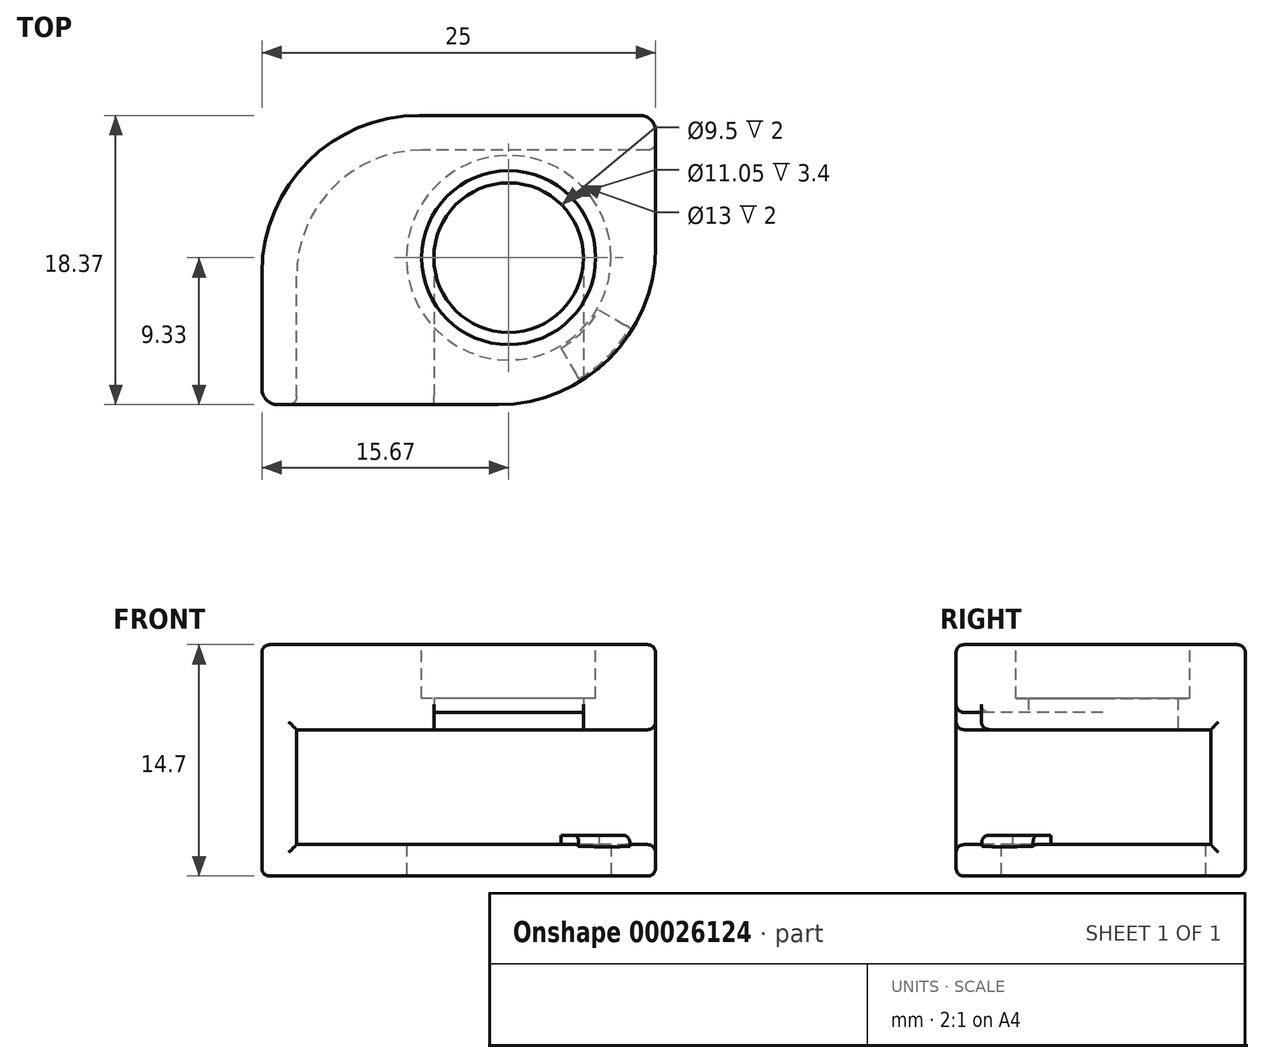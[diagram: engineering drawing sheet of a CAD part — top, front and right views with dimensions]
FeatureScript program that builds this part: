
annotation { "Feature Type Name" : "Feature", "Feature Type Description" : "" }
export const myFeature = defineFeature(function(context is Context, id is Id, definition is map)
    precondition{}
    {
        {
            var Q0;
            Q0=qCreatedBy(makeId("Top.planeOp"),FACE);
            var sketch = newSketch(context, id + "F0", { "sketchPlane" : qUnion([Q0])});
            skCircle(sketch, "E0", {"center": v(0, 0) * mm, "radius": 4.75 * mm});
            skLineSegment(sketch, "E1.bottom", {"start": v(-15.67, 9.04) * mm, "end": v(9.33, 9.04) * mm});
            skLineSegment(sketch, "E1.top", {"start": v(-15.67, -9.33) * mm, "end": v(9.33, -9.33) * mm});
            skLineSegment(sketch, "E1.left", {"start": v(-15.67, 9.04) * mm, "end": v(-15.67, -9.33) * mm});
            skLineSegment(sketch, "E1.right", {"start": v(9.33, 9.04) * mm, "end": v(9.33, -9.33) * mm});
            skSolve(sketch);
        }
        {
            var Q0;
            Q0 = qSketchRegion(id + "F0", true);
            extrude(context, id + "F1", {"entities" : qUnion([Q0]), "depth" : 5.4 * mm});
        }
        {
            var Q0;
            Q0=makeQuery(id+"F1.opExtrude","CAP_FACE",FACE,{"disambiguationData":[OSD([sQuery(id+"F0.wireOp",EDGE,"E0"),sQuery(id+"F0.wireOp",EDGE,"E1.bottom"),sQuery(id+"F0.wireOp",EDGE,"E1.top"),sQuery(id+"F0.wireOp",EDGE,"E1.left"),sQuery(id+"F0.wireOp",EDGE,"E1.right")])],"isStart":false});
            var sketch = newSketch(context, id + "F2", { "sketchPlane" : qUnion([Q0])});
            skCircle(sketch, "E2", {"center": v(0, 0) * mm, "radius": 5.53 * mm});
            skSolve(sketch);
        }
        {
            var Q0;
            Q0 = qSketchRegion(id + "F2", true);
            extrude(context, id + "F3", {"entities" : qUnion([Q0]), "operationType" : NewBodyOperationType.REMOVE, "oppositeDirection" : true, "depth" : 3.4 * mm});
        }
        {
            var Q0;
            Q0=makeQuery(id+"F1.opExtrude","SWEPT_EDGE",EDGE,{"disambiguationData":[OSD([sQuery(id+"F0.wireOp",EDGE,"E1.top"),sQuery(id+"F0.wireOp",EDGE,"E1.right")])]});
            fillet(context, id + "F4", {"entities" : qUnion([Q0]), "radius" : 10 * mm, "tangentPropagation" : true, "allowEdgeOverflow" : false});
        }
        {
            var Q0;
            Q0=makeQuery(id+"F1.opExtrude","CAP_FACE",FACE,{"disambiguationData":[OSD([sQuery(id+"F0.wireOp",EDGE,"E0"),sQuery(id+"F0.wireOp",EDGE,"E1.bottom"),sQuery(id+"F0.wireOp",EDGE,"E1.top"),sQuery(id+"F0.wireOp",EDGE,"E1.left"),sQuery(id+"F0.wireOp",EDGE,"E1.right")])],"isStart":true});
            var sketch = newSketch(context, id + "F5", { "sketchPlane" : qUnion([Q0])});
            skLineSegment(sketch, "E3.bottom", {"start": v(9.33, -9.04) * mm, "end": v(-15.67, -9.04) * mm});
            skLineSegment(sketch, "E3.top", {"start": v(9.33, -6.84) * mm, "end": v(-13.47, -6.84) * mm});
            skLineSegment(sketch, "E3.left", {"start": v(9.33, -9.04) * mm, "end": v(9.33, -6.84) * mm});
            skLineSegment(sketch, "E3.right", {"start": v(-15.67, -9.04) * mm, "end": v(-15.67, -6.84) * mm});
            skLineSegment(sketch, "E4.bottom", {"start": v(-15.67, 9.33) * mm, "end": v(-13.47, 9.33) * mm});
            skLineSegment(sketch, "E4.left", {"start": v(-15.67, 9.33) * mm, "end": v(-15.67, -6.84) * mm});
            skLineSegment(sketch, "E4.right", {"start": v(-13.47, 9.33) * mm, "end": v(-13.47, -6.84) * mm});
            skSolve(sketch);
        }
        {
            var Q0;
            Q0 = qSketchRegion(id + "F5", true);
            extrude(context, id + "F6", {"entities" : qUnion([Q0]), "operationType" : NewBodyOperationType.ADD, "depth" : 7.3 * mm});
        }
        {
            var Q0;
            Q0=makeQuery(id+"F6.opExtrude","SWEPT_EDGE",EDGE,{"disambiguationData":[OSD([sQuery(id+"F5.wireOp",EDGE,"E3.top"),sQuery(id+"F5.wireOp",EDGE,"E4.right")])]});
            fillet(context, id + "F7", {"entities" : qUnion([Q0]), "radius" : 8 * mm, "tangentPropagation" : true, "allowEdgeOverflow" : false});
        }
        {
            var Q0;
            Q0=makeQuery(id+"F6.opExtrude","CAP_FACE",FACE,{"disambiguationData":[OSD([sQuery(id+"F5.wireOp",EDGE,"E3.bottom"),sQuery(id+"F5.wireOp",EDGE,"E3.top"),sQuery(id+"F5.wireOp",EDGE,"E3.left"),sQuery(id+"F5.wireOp",EDGE,"E3.right"),sQuery(id+"F5.wireOp",EDGE,"E4.bottom"),sQuery(id+"F5.wireOp",EDGE,"E4.left"),sQuery(id+"F5.wireOp",EDGE,"E4.right")])],"isStart":false});
            var sketch = newSketch(context, id + "F8", { "sketchPlane" : qUnion([Q0])});
            skLineSegment(sketch, "E5.bottom", {"start": v(-15.67, -9.04) * mm, "end": v(9.33, -9.04) * mm});
            skLineSegment(sketch, "E5.top", {"start": v(-15.67, 9.33) * mm, "end": v(9.33, 9.33) * mm});
            skLineSegment(sketch, "E5.left", {"start": v(-15.67, -9.04) * mm, "end": v(-15.67, 9.33) * mm});
            skLineSegment(sketch, "E5.right", {"start": v(9.33, -9.04) * mm, "end": v(9.33, 9.33) * mm});
            skSolve(sketch);
        }
        {
            var Q0;
            Q0 = qSketchRegion(id + "F8", true);
            extrude(context, id + "F9", {"entities" : qUnion([Q0]), "operationType" : NewBodyOperationType.ADD, "depth" : 2 * mm});
        }
        {
            var Q0;
            Q0=makeQuery(id+"F9.opExtrude","SWEPT_EDGE",EDGE,{"disambiguationData":[OSD([sQuery(id+"F8.wireOp",EDGE,"E5.top"),sQuery(id+"F8.wireOp",EDGE,"E5.right")])]});
            var Q1;
            Q1=makeQuery(id+"F9.boolean.opBoolean","MERGE",EDGE,{"derivedFrom":[makeQuery(id+"F6.boolean.opBoolean","MERGE",EDGE,{"derivedFrom":[makeQuery(id+"F1.opExtrude","SWEPT_EDGE",EDGE,{"disambiguationData":[OSD([sQuery(id+"F0.wireOp",EDGE,"E1.bottom"),sQuery(id+"F0.wireOp",EDGE,"E1.left")])]}),makeQuery(id+"F6.opExtrude","SWEPT_EDGE",EDGE,{"disambiguationData":[OSD([sQuery(id+"F5.wireOp",EDGE,"E3.bottom"),sQuery(id+"F5.wireOp",EDGE,"E3.right")])]})]}),makeQuery(id+"F9.opExtrude","SWEPT_EDGE",EDGE,{"disambiguationData":[OSD([sQuery(id+"F8.wireOp",EDGE,"E5.bottom"),sQuery(id+"F8.wireOp",EDGE,"E5.left")])]})]});
            fillet(context, id + "F10", {"entities" : qUnion([Q0, Q1]), "radius" : 10 * mm, "tangentPropagation" : true, "allowEdgeOverflow" : false});
        }
        {
            var Q0;
            Q0=makeQuery(id+"F9.opExtrude","CAP_FACE",FACE,{"disambiguationData":[OSD([sQuery(id+"F8.wireOp",EDGE,"E5.bottom"),sQuery(id+"F8.wireOp",EDGE,"E5.top"),sQuery(id+"F8.wireOp",EDGE,"E5.left"),sQuery(id+"F8.wireOp",EDGE,"E5.right")])],"isStart":false});
            var sketch = newSketch(context, id + "F11", { "sketchPlane" : qUnion([Q0])});
            skCircle(sketch, "E6", {"center": v(0, 0) * mm, "radius": 6.5 * mm});
            skSolve(sketch);
        }
        {
            var Q0;
            Q0 = qSketchRegion(id + "F11", true);
            extrude(context, id + "F12", {"entities" : qUnion([Q0]), "operationType" : NewBodyOperationType.REMOVE, "endBound" : BoundingType.UP_TO_NEXT, "oppositeDirection" : true, "depth" : 25 * mm});
        }
        {
            var Q0;
            Q0=makeQuery(id+"F1.opExtrude","CAP_FACE",FACE,{"disambiguationData":[OSD([sQuery(id+"F0.wireOp",EDGE,"E0"),sQuery(id+"F0.wireOp",EDGE,"E1.bottom"),sQuery(id+"F0.wireOp",EDGE,"E1.top"),sQuery(id+"F0.wireOp",EDGE,"E1.left"),sQuery(id+"F0.wireOp",EDGE,"E1.right")])],"isStart":true});
            var sketch = newSketch(context, id + "F13", { "sketchPlane" : qUnion([Q0])});
            skLineSegment(sketch, "E7.bottom", {"start": v(0, 0) * mm, "end": v(-4.75, 0) * mm});
            skLineSegment(sketch, "E7.top", {"start": v(0, 12.5) * mm, "end": v(-4.75, 12.5) * mm});
            skLineSegment(sketch, "E7.right", {"start": v(-4.75, 0) * mm, "end": v(-4.75, 12.5) * mm});
            skLineSegment(sketch, "E8.bottom", {"start": v(0, 0) * mm, "end": v(4.75, 0) * mm});
            skLineSegment(sketch, "E8.top", {"start": v(0, 12.5) * mm, "end": v(4.75, 12.5) * mm});
            skLineSegment(sketch, "E8.right", {"start": v(4.75, 0) * mm, "end": v(4.75, 12.5) * mm});
            skSolve(sketch);
        }
        {
            var Q0;
            Q0 = qSketchRegion(id + "F13", true);
            extrude(context, id + "F14", {"entities" : qUnion([Q0]), "operationType" : NewBodyOperationType.REMOVE, "oppositeDirection" : true, "depth" : 1.1 * mm});
        }
        {
            var Q0;
            Q0=makeQuery(id+"F9.opExtrude","CAP_FACE",FACE,{"disambiguationData":[OSD([sQuery(id+"F8.wireOp",EDGE,"E5.bottom"),sQuery(id+"F8.wireOp",EDGE,"E5.top"),sQuery(id+"F8.wireOp",EDGE,"E5.left"),sQuery(id+"F8.wireOp",EDGE,"E5.right")])],"isStart":true});
            var sketch = newSketch(context, id + "F15", { "sketchPlane" : qUnion([Q0])});
            skLineSegment(sketch, "E9", {"start": v(3.32, -5.75) * mm, "end": v(4.45, -7.7) * mm});
            skLineSegment(sketch, "E10", {"start": v(5.75, -3.32) * mm, "end": v(7.7, -4.45) * mm});
            skArc(sketch, "E11", {"start": v(4.45, -7.7) * mm, "mid": v(6.29, -6.29) * mm, "end": v(7.7, -4.45) * mm});
            skArc(sketch, "E12", {"start": v(3.32, -5.75) * mm, "mid": v(4.7, -4.7) * mm, "end": v(5.75, -3.32) * mm});
            skPoint(sketch, "E13", {"position": v(3.32, -5.75) * mm});
            skPoint(sketch, "E14", {"position": v(5.75, -3.32) * mm});
            skPoint(sketch, "E15", {"position": v(7.7, -4.45) * mm});
            skPoint(sketch, "E16", {"position": v(4.45, -7.7) * mm});
            skSolve(sketch);
        }
        {
            var Q0;
            Q0 = qSketchRegion(id + "F15", true);
            extrude(context, id + "F16", {"entities" : qUnion([Q0]), "operationType" : NewBodyOperationType.ADD, "depth" : .6 * mm});
        }
        {
            var Q0;
            {var subQ0=sQuery(id+"F8.wireOp",EDGE,"E5.bottom");var subQ1=sQuery(id+"F8.wireOp",EDGE,"E5.left");Q0=makeQuery(id+"F10.opFillet","BLEND_EDGE",EDGE,{"blendedFrom":[makeQuery(id+"F9.boolean.opBoolean","MERGE",EDGE,{"derivedFrom":[makeQuery(id+"F6.boolean.opBoolean","MERGE",EDGE,{"derivedFrom":[makeQuery(id+"F1.opExtrude","SWEPT_EDGE",EDGE,{"disambiguationData":[OSD([sQuery(id+"F0.wireOp",EDGE,"E1.bottom"),sQuery(id+"F0.wireOp",EDGE,"E1.left")])]}),makeQuery(id+"F6.opExtrude","SWEPT_EDGE",EDGE,{"disambiguationData":[OSD([sQuery(id+"F5.wireOp",EDGE,"E3.bottom"),sQuery(id+"F5.wireOp",EDGE,"E3.right")])]})]}),makeQuery(id+"F9.opExtrude","SWEPT_EDGE",EDGE,{"disambiguationData":[OSD([subQ0,subQ1])]})]}),makeQuery(id+"F9.opExtrude","CAP_FACE",FACE,{"disambiguationData":[OSD([subQ0,sQuery(id+"F8.wireOp",EDGE,"E5.top"),subQ1,sQuery(id+"F8.wireOp",EDGE,"E5.right")])],"isStart":false})],"blendedInto":[makeQuery(id+"F9.opExtrude","CAP_FACE",FACE,{"disambiguationData":[OSD([subQ0,sQuery(id+"F8.wireOp",EDGE,"E5.top"),subQ1,sQuery(id+"F8.wireOp",EDGE,"E5.right")])],"isStart":false})]});}
            var Q1;
            Q1=makeQuery(id+"F9.opExtrude","CAP_EDGE",EDGE,{"disambiguationData":[OSD([sQuery(id+"F8.wireOp",EDGE,"E5.bottom")])],"isStart":false});
            var Q2;
            Q2=makeQuery(id+"F9.opExtrude","CAP_EDGE",EDGE,{"disambiguationData":[OSD([sQuery(id+"F8.wireOp",EDGE,"E5.left")])],"isStart":false});
            var Q3;
            Q3=makeQuery(id+"F9.opExtrude","CAP_EDGE",EDGE,{"disambiguationData":[OSD([sQuery(id+"F8.wireOp",EDGE,"E5.right")])],"isStart":false});
            var Q4;
            {var subQ0=sQuery(id+"F8.wireOp",EDGE,"E5.top");var subQ1=sQuery(id+"F8.wireOp",EDGE,"E5.right");Q4=makeQuery(id+"F10.opFillet","BLEND_EDGE",EDGE,{"blendedFrom":[makeQuery(id+"F9.opExtrude","SWEPT_EDGE",EDGE,{"disambiguationData":[OSD([subQ0,subQ1])]}),makeQuery(id+"F9.opExtrude","CAP_FACE",FACE,{"disambiguationData":[OSD([sQuery(id+"F8.wireOp",EDGE,"E5.bottom"),subQ0,sQuery(id+"F8.wireOp",EDGE,"E5.left"),subQ1])],"isStart":false})],"blendedInto":[makeQuery(id+"F9.opExtrude","CAP_FACE",FACE,{"disambiguationData":[OSD([sQuery(id+"F8.wireOp",EDGE,"E5.bottom"),subQ0,sQuery(id+"F8.wireOp",EDGE,"E5.left"),subQ1])],"isStart":false})]});}
            var Q5;
            Q5=makeQuery(id+"F1.opExtrude","CAP_EDGE",EDGE,{"disambiguationData":[OSD([sQuery(id+"F0.wireOp",EDGE,"E1.top")])],"isStart":false});
            var Q6;
            {var subQ0=sQuery(id+"F0.wireOp",EDGE,"E1.bottom");var subQ1=sQuery(id+"F0.wireOp",EDGE,"E1.left");Q6=makeQuery(id+"F10.opFillet","BLEND_EDGE",EDGE,{"blendedFrom":[makeQuery(id+"F9.boolean.opBoolean","MERGE",EDGE,{"derivedFrom":[makeQuery(id+"F6.boolean.opBoolean","MERGE",EDGE,{"derivedFrom":[makeQuery(id+"F1.opExtrude","SWEPT_EDGE",EDGE,{"disambiguationData":[OSD([subQ0,subQ1])]}),makeQuery(id+"F6.opExtrude","SWEPT_EDGE",EDGE,{"disambiguationData":[OSD([sQuery(id+"F5.wireOp",EDGE,"E3.bottom"),sQuery(id+"F5.wireOp",EDGE,"E3.right")])]})]}),makeQuery(id+"F9.opExtrude","SWEPT_EDGE",EDGE,{"disambiguationData":[OSD([sQuery(id+"F8.wireOp",EDGE,"E5.bottom"),sQuery(id+"F8.wireOp",EDGE,"E5.left")])]})]}),makeQuery(id+"F1.opExtrude","CAP_FACE",FACE,{"disambiguationData":[OSD([sQuery(id+"F0.wireOp",EDGE,"E0"),subQ0,sQuery(id+"F0.wireOp",EDGE,"E1.top"),subQ1,sQuery(id+"F0.wireOp",EDGE,"E1.right")])],"isStart":false})],"blendedInto":[makeQuery(id+"F1.opExtrude","CAP_FACE",FACE,{"disambiguationData":[OSD([sQuery(id+"F0.wireOp",EDGE,"E0"),subQ0,sQuery(id+"F0.wireOp",EDGE,"E1.top"),subQ1,sQuery(id+"F0.wireOp",EDGE,"E1.right")])],"isStart":false})]});}
            var Q7;
            Q7=makeQuery(id+"F12.boolean.opBoolean","COPY",EDGE,{"derivedFrom":makeQuery(id+"F12.opExtrude","CAP_EDGE",EDGE,{"disambiguationData":[OSD([sQuery(id+"F11.wireOp",EDGE,"E6")])],"isStart":true})});
            var Q8;
            Q8=makeQuery(id+"F3.boolean.opBoolean","COPY",EDGE,{"derivedFrom":makeQuery(id+"F3.opExtrude","CAP_EDGE",EDGE,{"disambiguationData":[OSD([sQuery(id+"F2.wireOp",EDGE,"E2")])],"isStart":true})});
            var Q9;
            {var subQ0=sQuery(id+"F0.wireOp",EDGE,"E1.top");var subQ1=sQuery(id+"F0.wireOp",EDGE,"E1.right");Q9=makeQuery(id+"F4.opFillet","BLEND_EDGE",EDGE,{"blendedFrom":[makeQuery(id+"F1.opExtrude","SWEPT_EDGE",EDGE,{"disambiguationData":[OSD([subQ0,subQ1])]}),makeQuery(id+"F1.opExtrude","CAP_FACE",FACE,{"disambiguationData":[OSD([sQuery(id+"F0.wireOp",EDGE,"E0"),sQuery(id+"F0.wireOp",EDGE,"E1.bottom"),subQ0,sQuery(id+"F0.wireOp",EDGE,"E1.left"),subQ1])],"isStart":true})],"blendedInto":[makeQuery(id+"F1.opExtrude","CAP_FACE",FACE,{"disambiguationData":[OSD([sQuery(id+"F0.wireOp",EDGE,"E0"),sQuery(id+"F0.wireOp",EDGE,"E1.bottom"),subQ0,sQuery(id+"F0.wireOp",EDGE,"E1.left"),subQ1])],"isStart":true})]});}
            var Q10;
            Q10=makeQuery(id+"F1.opExtrude","CAP_EDGE",EDGE,{"disambiguationData":[OSD([sQuery(id+"F0.wireOp",EDGE,"E1.top")])],"isStart":true});
            var Q11;
            Q11=makeQuery(id+"F9.opExtrude","CAP_EDGE",EDGE,{"disambiguationData":[OSD([sQuery(id+"F8.wireOp",EDGE,"E5.top")])],"isStart":true});
            var Q12;
            Q12=makeQuery(id+"F16.opExtrude","CAP_EDGE",EDGE,{"disambiguationData":[OSD([sQuery(id+"F15.wireOp",EDGE,"E11")])],"isStart":false});
            var Q13;
            Q13=makeQuery(id+"F14.boolean.opBoolean","INTERSECT",EDGE,{"derivedFrom":[makeQuery(id+"F4.opFillet","BLEND_FACE",FACE,{"disambiguationData":[OSD([sQuery(id+"F0.wireOp",EDGE,"E1.top"),sQuery(id+"F0.wireOp",EDGE,"E1.right")])]}),makeQuery(id+"F14.opExtrude","CAP_FACE",FACE,{"disambiguationData":[OSD([sQuery(id+"F13.wireOp",EDGE,"E7.bottom"),sQuery(id+"F13.wireOp",EDGE,"E7.top"),sQuery(id+"F13.wireOp",EDGE,"E7.right"),sQuery(id+"F13.wireOp",EDGE,"E8.bottom"),sQuery(id+"F13.wireOp",EDGE,"E8.top"),sQuery(id+"F13.wireOp",EDGE,"E8.right")])],"isStart":false})]});
            var Q14;
            Q14=makeQuery(id+"F6.opExtrude","SWEPT_EDGE",EDGE,{"disambiguationData":[OSD([sQuery(id+"F0.wireOp",EDGE,"E1.right"),sQuery(id+"F5.wireOp",EDGE,"E3.top"),sQuery(id+"F5.wireOp",EDGE,"E3.left")])]});
            var Q15;
            Q15=makeQuery(id+"F6.opExtrude","SWEPT_EDGE",EDGE,{"disambiguationData":[OSD([sQuery(id+"F0.wireOp",EDGE,"E1.top"),sQuery(id+"F5.wireOp",EDGE,"E4.bottom"),sQuery(id+"F5.wireOp",EDGE,"E4.right")])]});
            fillet(context, id + "F17", {"entities" : qUnion([Q0, Q1, Q2, Q3, Q4, Q5, Q6, Q7, Q8, Q9, Q10, Q11, Q12, Q13, Q14, Q15]), "radius" : .5 * mm, "tangentPropagation" : true, "allowEdgeOverflow" : false});
        }
        {
            var Q0;
            Q0=makeQuery(id+"F9.boolean.opBoolean","MERGE",EDGE,{"derivedFrom":[makeQuery(id+"F6.boolean.opBoolean","MERGE",EDGE,{"derivedFrom":[makeQuery(id+"F1.opExtrude","SWEPT_EDGE",EDGE,{"disambiguationData":[OSD([sQuery(id+"F0.wireOp",EDGE,"E1.top"),sQuery(id+"F0.wireOp",EDGE,"E1.left")])]}),makeQuery(id+"F6.opExtrude","SWEPT_EDGE",EDGE,{"disambiguationData":[OSD([sQuery(id+"F5.wireOp",EDGE,"E4.bottom"),sQuery(id+"F5.wireOp",EDGE,"E4.left")])]})]}),makeQuery(id+"F9.opExtrude","SWEPT_EDGE",EDGE,{"disambiguationData":[OSD([sQuery(id+"F8.wireOp",EDGE,"E5.top"),sQuery(id+"F8.wireOp",EDGE,"E5.left")])]})]});
            var Q1;
            Q1=makeQuery(id+"F9.boolean.opBoolean","MERGE",EDGE,{"derivedFrom":[makeQuery(id+"F6.boolean.opBoolean","MERGE",EDGE,{"derivedFrom":[makeQuery(id+"F1.opExtrude","SWEPT_EDGE",EDGE,{"disambiguationData":[OSD([sQuery(id+"F0.wireOp",EDGE,"E1.bottom"),sQuery(id+"F0.wireOp",EDGE,"E1.right")])]}),makeQuery(id+"F6.opExtrude","SWEPT_EDGE",EDGE,{"disambiguationData":[OSD([sQuery(id+"F5.wireOp",EDGE,"E3.bottom"),sQuery(id+"F5.wireOp",EDGE,"E3.left")])]})]}),makeQuery(id+"F9.opExtrude","SWEPT_EDGE",EDGE,{"disambiguationData":[OSD([sQuery(id+"F8.wireOp",EDGE,"E5.bottom"),sQuery(id+"F8.wireOp",EDGE,"E5.right")])]})]});
            fillet(context, id + "F18", {"entities" : qUnion([Q0, Q1]), "radius" : 1 * mm, "tangentPropagation" : true, "allowEdgeOverflow" : false});
        }
    });
